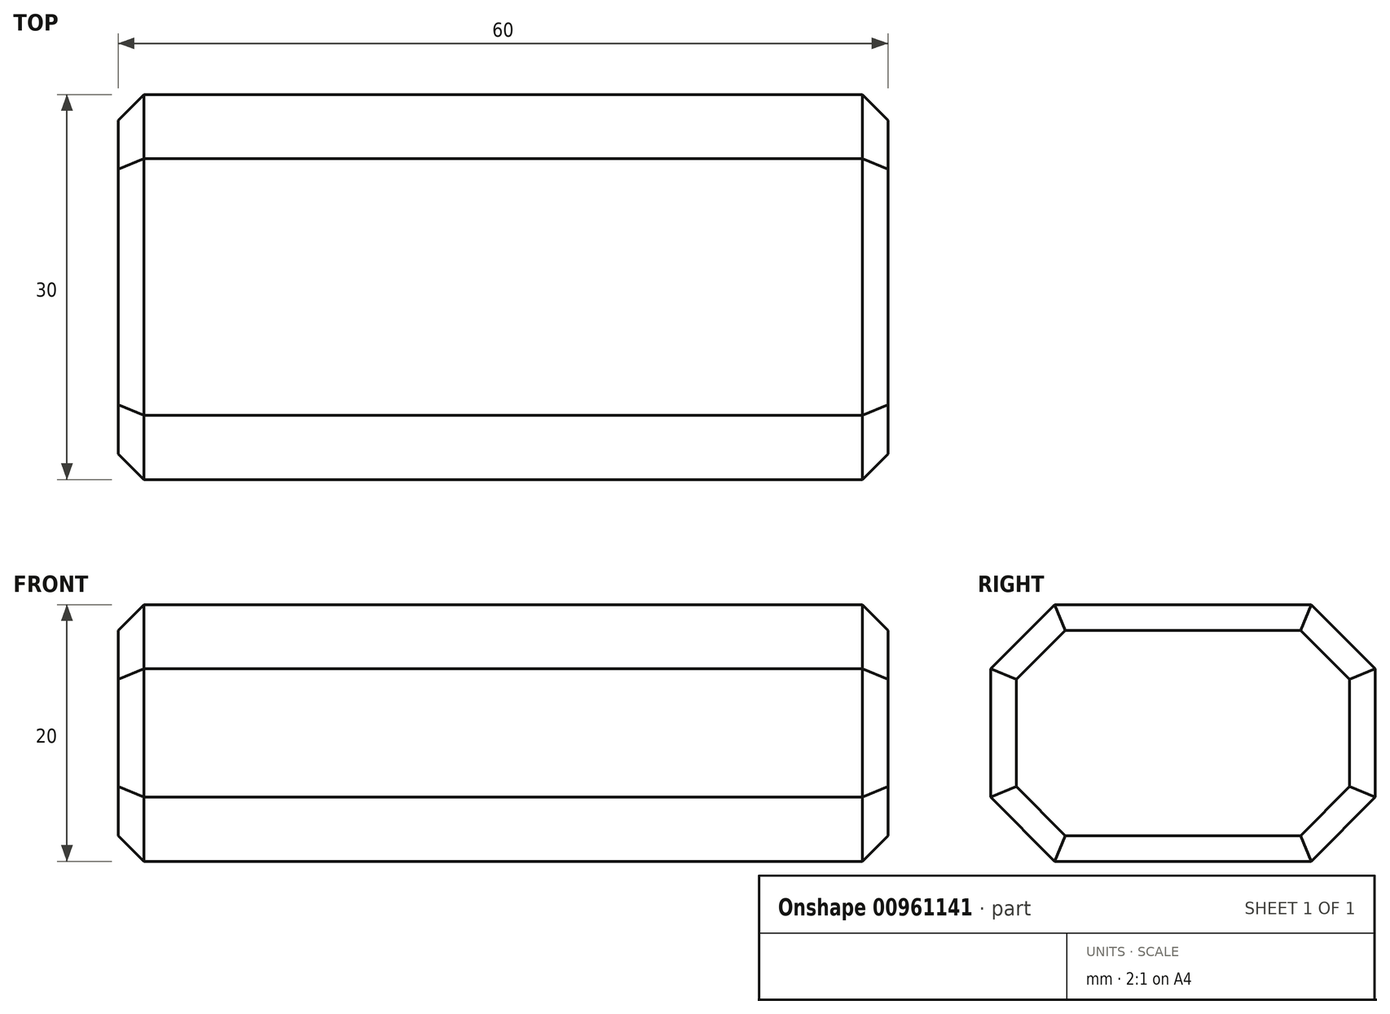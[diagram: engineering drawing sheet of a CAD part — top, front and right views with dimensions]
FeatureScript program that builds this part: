
annotation { "Feature Type Name" : "Feature", "Feature Type Description" : "" }
export const myFeature = defineFeature(function(context is Context, id is Id, definition is map)
    precondition{}
    {
        {
            var Q0;
            Q0=qCreatedBy(makeId("Top.planeOp"),FACE);
            var sketch = newSketch(context, id + "F0", { "sketchPlane" : qUnion([Q0])});
            skLineSegment(sketch, "E0.bottom", {"start": v(-30, 15) * mm, "end": v(30, 15) * mm});
            skLineSegment(sketch, "E0.top", {"start": v(-30, -15) * mm, "end": v(30, -15) * mm});
            skLineSegment(sketch, "E0.left", {"start": v(-30, 15) * mm, "end": v(-30, -15) * mm});
            skLineSegment(sketch, "E0.right", {"start": v(30, 15) * mm, "end": v(30, -15) * mm});
            skLineSegment(sketch, "E1", {"start": v(-30, 0) * mm, "end": v(30, 0) * mm, "construction": true});
            skLineSegment(sketch, "E2", {"start": v(0, 15) * mm, "end": v(0, -15) * mm, "construction": true});
            skPoint(sketch, "E3", {"position": v(0, 0) * mm});
            skSolve(sketch);
        }
        {
            var Q0;
            Q0 = qSketchRegion(id + "F0", true);
            extrude(context, id + "F1", {"entities" : qUnion([Q0]), "depth" : 20 * mm, "offsetDistance" : 25 * mm});
        }
        {
            var Q0;
            Q0=makeQuery(id+"F1.opExtrude","CAP_EDGE",EDGE,{"disambiguationData":[OSD([sQuery(id+"F0.wireOp",EDGE,"E0.top")])],"isStart":false});
            var Q1;
            Q1=makeQuery(id+"F1.opExtrude","CAP_EDGE",EDGE,{"disambiguationData":[OSD([sQuery(id+"F0.wireOp",EDGE,"E0.bottom")])],"isStart":false});
            var Q2;
            Q2=makeQuery(id+"F1.opExtrude","CAP_EDGE",EDGE,{"disambiguationData":[OSD([sQuery(id+"F0.wireOp",EDGE,"E0.top")])],"isStart":true});
            var Q3;
            Q3=makeQuery(id+"F1.opExtrude","CAP_EDGE",EDGE,{"disambiguationData":[OSD([sQuery(id+"F0.wireOp",EDGE,"E0.bottom")])],"isStart":true});
            chamfer(context, id + "F2", {"entities" : qUnion([Q0, Q1, Q2, Q3]), "width" : 5 * mm, "tangentPropagation" : true});
        }
        {
            var Q0;
            Q0=makeQuery(id+"F1.opExtrude","SWEPT_FACE",FACE,{"disambiguationData":[OSD([sQuery(id+"F0.wireOp",EDGE,"E0.right")])]});
            var Q1;
            Q1=makeQuery(id+"F1.opExtrude","SWEPT_FACE",FACE,{"disambiguationData":[OSD([sQuery(id+"F0.wireOp",EDGE,"E0.left")])]});
            chamfer(context, id + "F3", {"entities" : qUnion([Q0, Q1]), "width" : 2 * mm, "tangentPropagation" : true});
        }
    });
